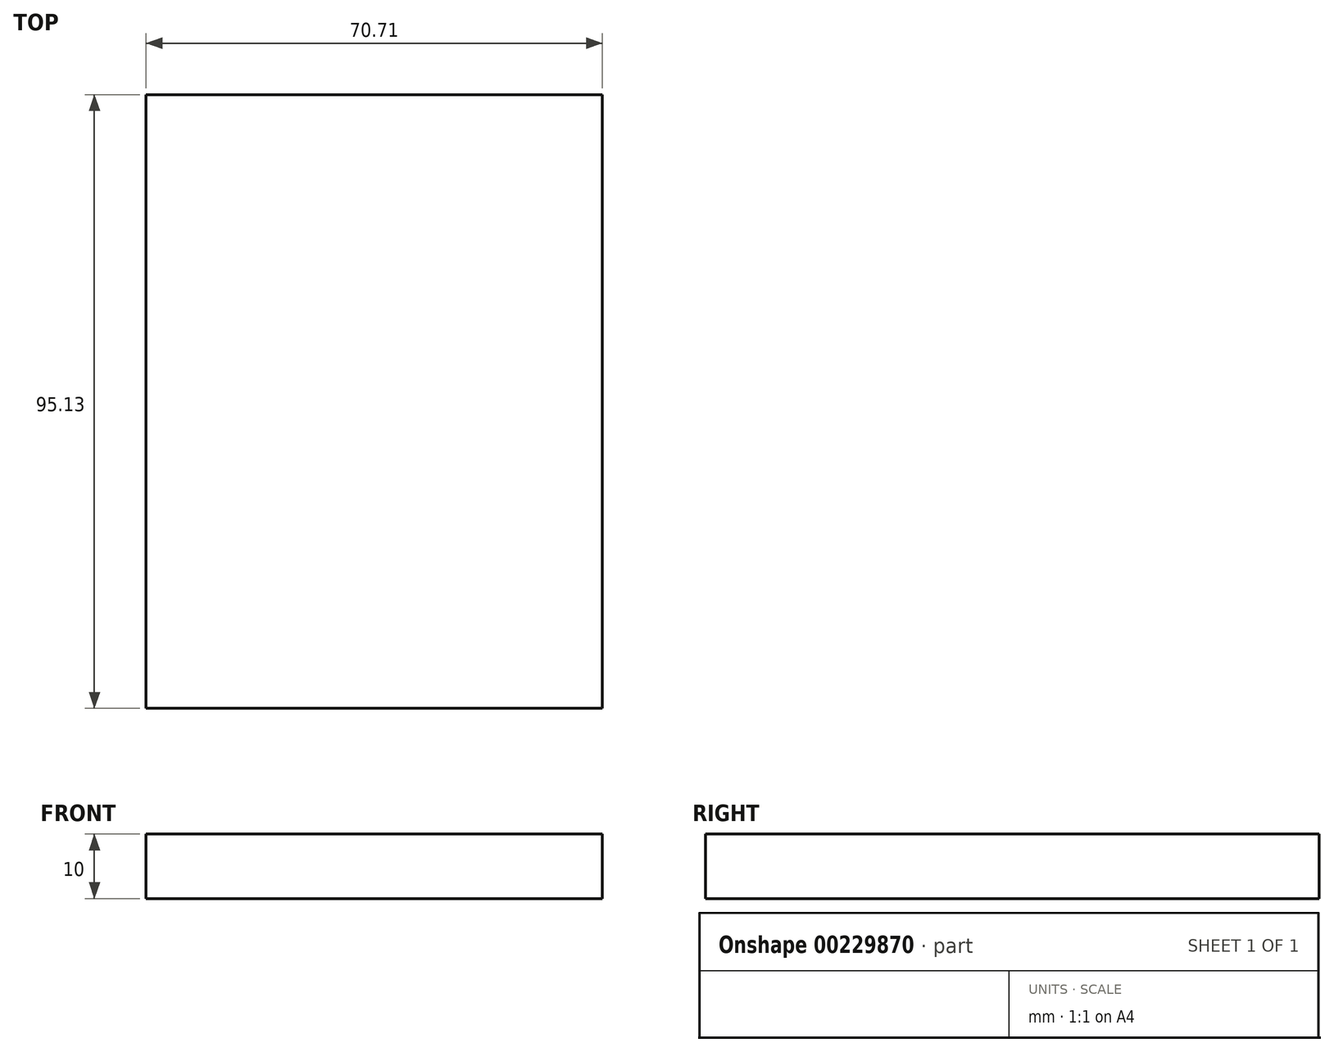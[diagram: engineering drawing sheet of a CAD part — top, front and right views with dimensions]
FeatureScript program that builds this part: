
annotation { "Feature Type Name" : "Feature", "Feature Type Description" : "" }
export const myFeature = defineFeature(function(context is Context, id is Id, definition is map)
    precondition{}
    {
        {
            var Q0;
            Q0=qCreatedBy(makeId("Top.planeOp"),FACE);
            var sketch = newSketch(context, id + "F0", { "sketchPlane" : qUnion([Q0])});
            skLineSegment(sketch, "E0.bottom", {"start": v(-35.33, -48) * mm, "end": v(35.38, -48) * mm});
            skLineSegment(sketch, "E0.top", {"start": v(-35.33, 47.12) * mm, "end": v(35.38, 47.12) * mm});
            skLineSegment(sketch, "E0.left", {"start": v(-35.33, -48) * mm, "end": v(-35.33, 47.12) * mm});
            skLineSegment(sketch, "E0.right", {"start": v(35.38, -48) * mm, "end": v(35.38, 47.12) * mm});
            skSolve(sketch);
        }
        {
            var Q0;
            Q0=makeQuery(id+"F0.imprint","IMPRINT",FACE,{"disambiguationData":[TD([[makeQuery(id+"F0.imprint","IMPRINT",EDGE,{"derivedFrom":sQuery(id+"F0.wireOp",EDGE,"E0.bottom")}),1.0]])]});
            extrude(context, id + "F1", {"entities" : qUnion([Q0]), "depth" : 10 * mm});
        }
    });
